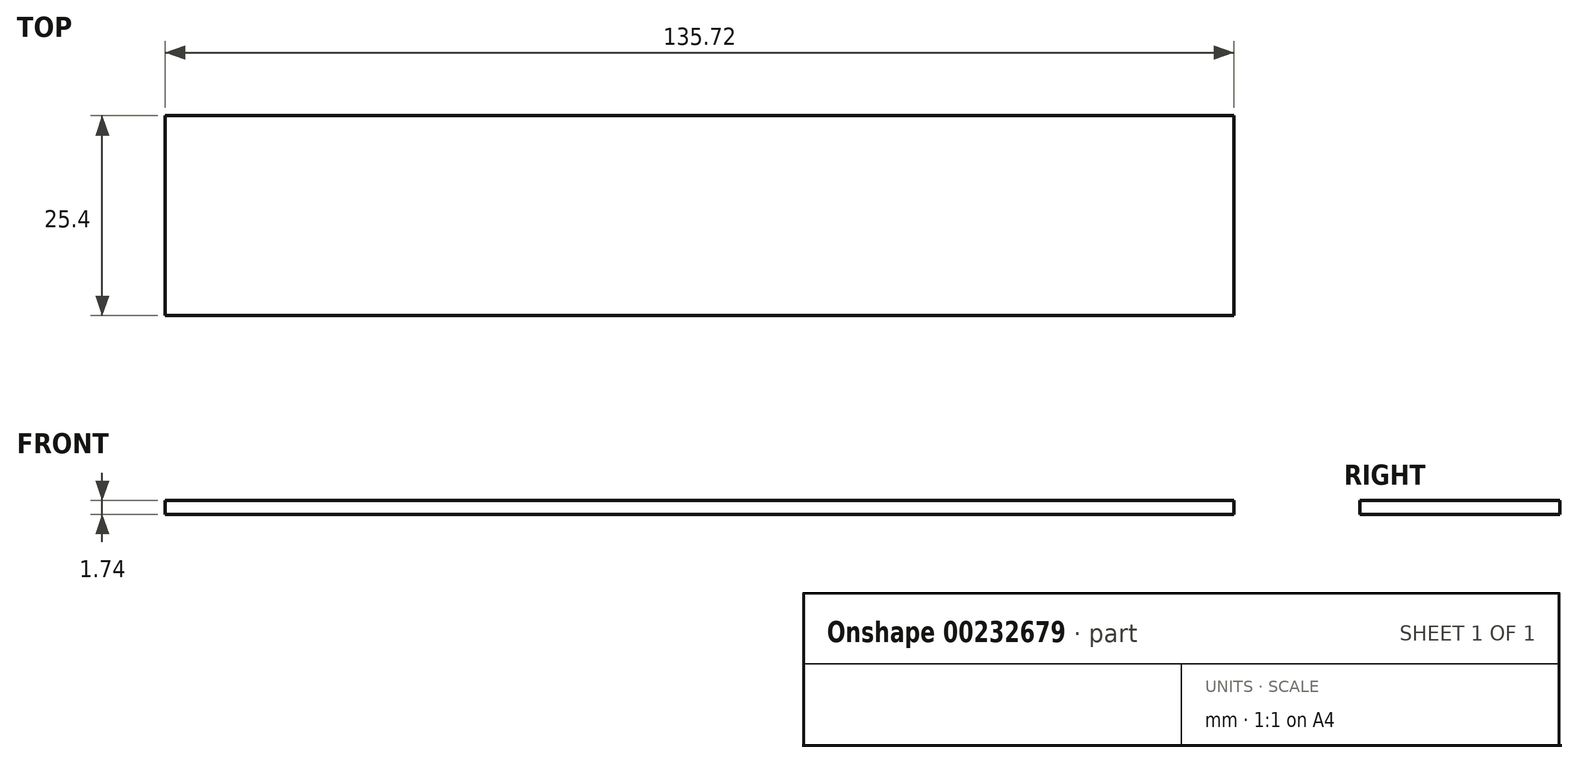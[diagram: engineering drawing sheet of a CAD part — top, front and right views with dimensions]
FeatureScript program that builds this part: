
annotation { "Feature Type Name" : "Feature", "Feature Type Description" : "" }
export const myFeature = defineFeature(function(context is Context, id is Id, definition is map)
    precondition{}
    {
        {
            var Q0;
            Q0=qCreatedBy(makeId("Front.planeOp"),FACE);
            var sketch = newSketch(context, id + "F0", { "sketchPlane" : qUnion([Q0])});
            skLineSegment(sketch, "E0.bottom", {"start": v(-55.69, 26.18) * mm, "end": v(20.51, 26.18) * mm});
            skLineSegment(sketch, "E0.top", {"start": v(-55.69, -38.4) * mm, "end": v(20.51, -38.4) * mm});
            skLineSegment(sketch, "E0.left", {"start": v(-55.69, 26.18) * mm, "end": v(-55.69, -38.4) * mm});
            skLineSegment(sketch, "E0.right", {"start": v(20.51, 26.18) * mm, "end": v(20.51, -38.4) * mm});
            skLineSegment(sketch, "E1.bottom", {"start": v(-73.75, -6.98) * mm, "end": v(-209.47, -6.98) * mm});
            skLineSegment(sketch, "E1.top", {"start": v(-73.75, -5.24) * mm, "end": v(-209.47, -5.24) * mm});
            skLineSegment(sketch, "E1.left", {"start": v(-73.75, -6.98) * mm, "end": v(-73.75, -5.24) * mm});
            skLineSegment(sketch, "E1.right", {"start": v(-209.47, -6.98) * mm, "end": v(-209.47, -5.24) * mm});
            skSolve(sketch);
        }
        {
            var Q0;
            Q0=makeQuery(id+"F0.imprint","IMPRINT",FACE,{"disambiguationData":[TD([[makeQuery(id+"F0.imprint","IMPRINT",EDGE,{"derivedFrom":sQuery(id+"F0.wireOp",EDGE,"E1.bottom")}),-1.0]])]});
            extrude(context, id + "F1", {"entities" : qUnion([Q0]), "depth" : 25.4 * mm});
        }
    });
